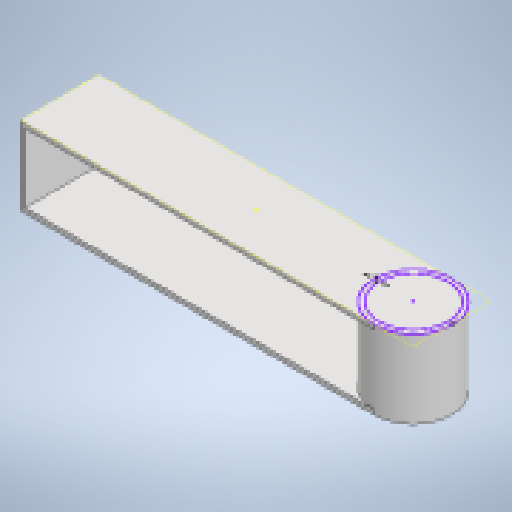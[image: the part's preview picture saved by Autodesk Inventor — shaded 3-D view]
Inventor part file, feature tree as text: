
AUTODESK INVENTOR PART (.ipt)
format: ipt  version: 2023 (Build 270158000, 158)  size: 194,560 bytes
history: native  units: mm
features: sketch x5, extrude x4, projected_geometry x4, other x1, shell x1, fillet x1
ambient origin geometry x8: Origin, YZ Plane, XZ Plane, XY Plane, X Axis, Y Axis, Z Axis, Center Point
bodies: Body1 (feature_tree)
feature tree (16):
  other  "實體1"
  extrude  "擠出1"  Depth=250.0mm
  shell  "薄殼1"  Thickness=50.0mm
  extrude  "擠出2"  Depth=50.0mm TaperAngle=0.0deg
  sketch  "草圖4"
  extrude  "擠出4"  Depth=3.0mm
  extrude  "擠出5"  Depth=3.0mm
  fillet  "圓角1"  Radius=50.0mm
  sketch  "草圖1"
  sketch  "草圖2"
  projected_geometry  "投影迴路1"
  sketch  "草圖5"
  projected_geometry  "投影迴路3"
  sketch  "草圖6"
  projected_geometry  "投影迴路4"
  projected_geometry  "投影迴路5"
